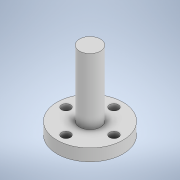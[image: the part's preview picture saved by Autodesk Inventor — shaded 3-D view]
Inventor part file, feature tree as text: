
AUTODESK INVENTOR PART (.ipt)
format: ipt  version: 2021 (Build 250183000, 183)  size: 119,808 bytes
history: native  units: mm
features: extrude x3, sketch x3, other x1
ambient origin geometry x8: Origin, YZ Plane, XZ Plane, XY Plane, X Axis, Y Axis, Z Axis, Center Point
bodies: Body1 (feature_tree)
feature tree (7):
  other  "Sólido1"
  extrude  "Extrusión1"  Depth=4.0mm TaperAngle=0.0deg
  extrude  "Extrusión2"  Depth=3.0mm
  extrude  "Extrusión3"  Depth=4.0mm TaperAngle=0.0deg
  sketch  "Boceto1"  dims[d0=22.0mm d1=4.0mm d2=0.0mm]
  sketch  "Boceto2"  dims[d3=16.0mm d4=3.0mm]
  sketch  "Boceto3"  dims[d5=40.0mm d7=360.0deg d9=4.0mm d10=0.0mm d11=7.0mm d12=22.0mm d13=0.0mm]
